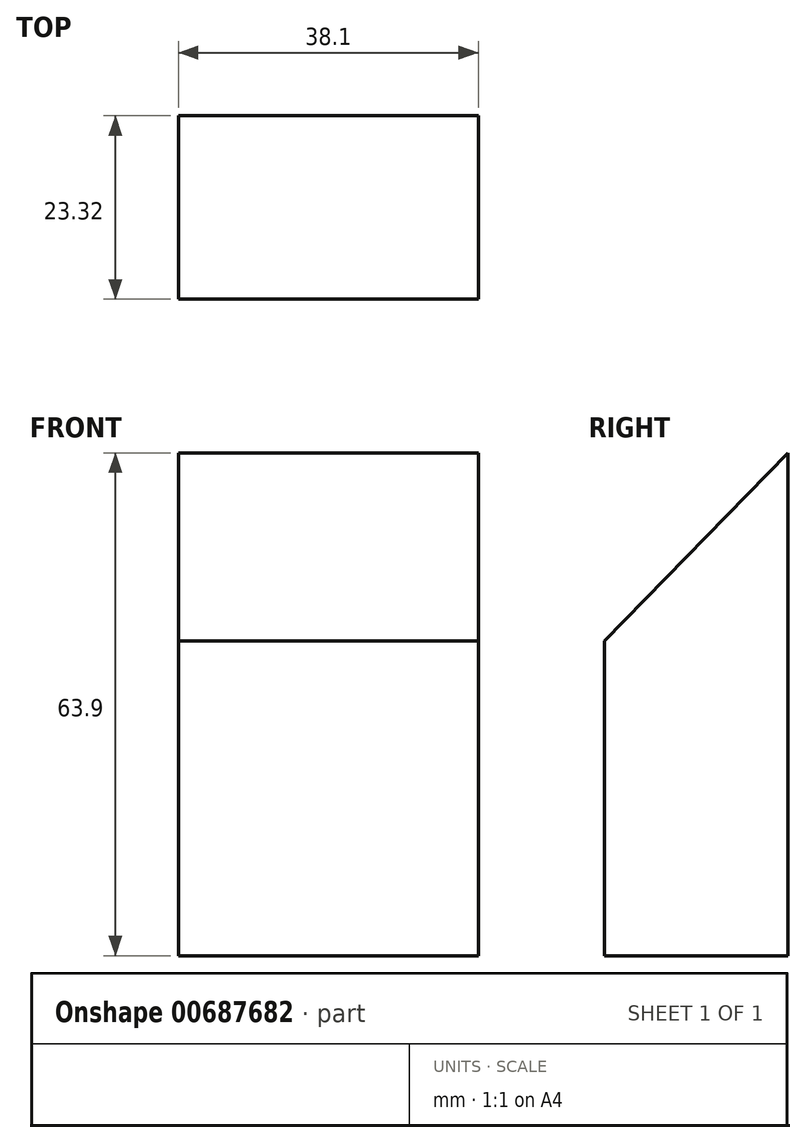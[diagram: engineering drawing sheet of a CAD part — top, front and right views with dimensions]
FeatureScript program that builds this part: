
annotation { "Feature Type Name" : "Feature", "Feature Type Description" : "" }
export const myFeature = defineFeature(function(context is Context, id is Id, definition is map)
    precondition{}
    {
        {
            var Q0;
            Q0=qCreatedBy(makeId("Right.planeOp"),FACE);
            var sketch = newSketch(context, id + "F0", { "sketchPlane" : qUnion([Q0])});
            skLineSegment(sketch, "E0", {"start": v(51.09, 39) * mm, "end": v(51.09, -24.9) * mm});
            skLineSegment(sketch, "E1", {"start": v(51.09, 39) * mm, "end": v(27.77, 15.1) * mm});
            skLineSegment(sketch, "E2", {"start": v(27.77, 15.1) * mm, "end": v(27.77, -24.9) * mm});
            skLineSegment(sketch, "E3", {"start": v(27.77, -24.9) * mm, "end": v(51.09, -24.9) * mm});
            skSolve(sketch);
        }
        {
            var Q0;
            Q0 = qSketchRegion(id + "F0", true);
            extrude(context, id + "F1", {"entities" : qUnion([Q0]), "depth" : 38.1 * mm, "offsetDistance" : 25.4 * mm});
        }
    });
